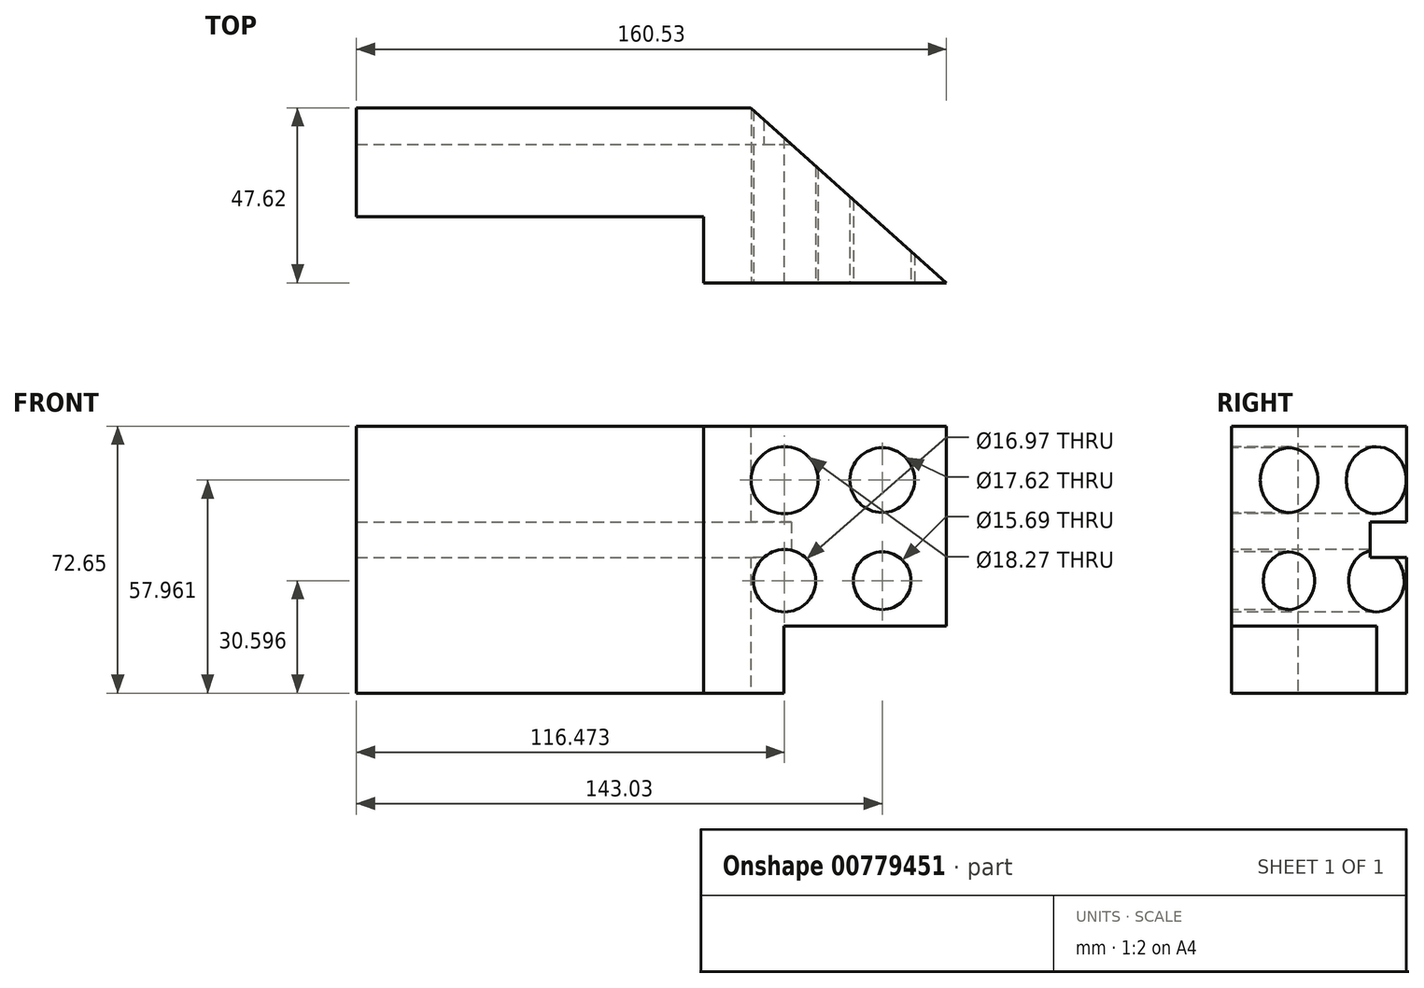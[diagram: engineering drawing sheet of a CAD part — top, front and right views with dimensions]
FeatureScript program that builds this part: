
annotation { "Feature Type Name" : "Feature", "Feature Type Description" : "" }
export const myFeature = defineFeature(function(context is Context, id is Id, definition is map)
    precondition{}
    {
        {
            var Q0;
            Q0=qCreatedBy(makeId("Top.planeOp"),FACE);
            var sketch = newSketch(context, id + "F0", { "sketchPlane" : qUnion([Q0])});
            skLineSegment(sketch, "E0.bottom", {"start": v(-53.64, 23.81) * mm, "end": v(53.64, 23.81) * mm});
            skLineSegment(sketch, "E0.top", {"start": v(-53.64, -23.81) * mm, "end": v(53.64, -23.81) * mm});
            skLineSegment(sketch, "E0.left", {"start": v(-53.64, 23.81) * mm, "end": v(-53.64, -23.81) * mm});
            skPoint(sketch, "E0.middle", {"position": v(0, 0) * mm});
            skLineSegment(sketch, "E1", {"start": v(53.64, -23.81) * mm, "end": v(106.9, -23.81) * mm});
            skLineSegment(sketch, "E2", {"start": v(106.9, -23.81) * mm, "end": v(53.64, 23.81) * mm});
            skSolve(sketch);
        }
        {
            var Q0;
            Q0=makeQuery(id+"F0.imprint","IMPRINT",FACE,{"disambiguationData":[TD([[makeQuery(id+"F0.imprint","IMPRINT",EDGE,{"derivedFrom":sQuery(id+"F0.wireOp",EDGE,"E0.bottom")}),-1.0]])]});
            extrude(context, id + "F1", {"entities" : qUnion([Q0]), "depth" : 54.36 * mm, "offsetDistance" : 25.4 * mm});
        }
        {
            var Q0;
            Q0=makeQuery(id+"F1.opExtrude","SWEPT_FACE",FACE,{"disambiguationData":[OSD([sQuery(id+"F0.wireOp",EDGE,"E0.top"),sQuery(id+"F0.wireOp",EDGE,"E1")])]});
            var sketch = newSketch(context, id + "F2", { "sketchPlane" : qUnion([Q0])});
            skLineSegment(sketch, "E3.bottom", {"start": v(-53.64, 54.36) * mm, "end": v(40.83, 54.36) * mm});
            skLineSegment(sketch, "E3.top", {"start": v(-53.64, 0) * mm, "end": v(40.83, 0) * mm});
            skLineSegment(sketch, "E3.left", {"start": v(-53.64, 54.36) * mm, "end": v(-53.64, 0) * mm});
            skLineSegment(sketch, "E3.right", {"start": v(40.83, 54.36) * mm, "end": v(40.83, 0) * mm});
            skSolve(sketch);
        }
        {
            var Q0;
            Q0=makeQuery(id+"F2.imprint","IMPRINT",FACE,{"disambiguationData":[TD([[makeQuery(id+"F2.imprint","IMPRINT",EDGE,{"derivedFrom":sQuery(id+"F2.wireOp",EDGE,"E3.bottom")}),-1.0]])]});
            extrude(context, id + "F3", {"entities" : qUnion([Q0]), "operationType" : NewBodyOperationType.REMOVE, "oppositeDirection" : true, "depth" : 18.03 * mm, "offsetDistance" : 25.4 * mm});
        }
        {
            var Q0;
            Q0=makeQuery(id+"F1.opExtrude","SWEPT_FACE",FACE,{"disambiguationData":[OSD([sQuery(id+"F0.wireOp",EDGE,"E0.top"),sQuery(id+"F0.wireOp",EDGE,"E1")])]});
            var sketch = newSketch(context, id + "F4", { "sketchPlane" : qUnion([Q0])});
            skPoint(sketch, "E4.middle", {"position": v(76.11, 25.99) * mm});
            skCircle(sketch, "E5", {"center": v(89.39, 39.67) * mm, "radius": 8.8 * mm});
            skCircle(sketch, "E6", {"center": v(89.39, 12.3) * mm, "radius": 7.85 * mm});
            skCircle(sketch, "E7", {"center": v(62.83, 12.3) * mm, "radius": 8.48 * mm});
            skCircle(sketch, "E8", {"center": v(62.83, 39.67) * mm, "radius": 9.14 * mm});
            skSolve(sketch);
        }
        {
            var Q0;
            Q0=makeQuery(id+"F4.imprint","IMPRINT",FACE,{"disambiguationData":[TD([[makeQuery(id+"F4.imprint","IMPRINT",EDGE,{"derivedFrom":sQuery(id+"F4.wireOp",EDGE,"E5")}),1.0]])]});
            var Q1;
            Q1=makeQuery(id+"F4.imprint","IMPRINT",FACE,{"disambiguationData":[TD([[makeQuery(id+"F4.imprint","IMPRINT",EDGE,{"derivedFrom":sQuery(id+"F4.wireOp",EDGE,"E6")}),1.0]])]});
            var Q2;
            Q2=makeQuery(id+"F4.imprint","IMPRINT",FACE,{"disambiguationData":[TD([[makeQuery(id+"F4.imprint","IMPRINT",EDGE,{"derivedFrom":sQuery(id+"F4.wireOp",EDGE,"E7")}),1.0]])]});
            var Q3;
            Q3=makeQuery(id+"F4.imprint","IMPRINT",FACE,{"disambiguationData":[TD([[makeQuery(id+"F4.imprint","IMPRINT",EDGE,{"derivedFrom":sQuery(id+"F4.wireOp",EDGE,"E8")}),1.0]])]});
            extrude(context, id + "F5", {"entities" : qUnion([Q0, Q1, Q2, Q3]), "operationType" : NewBodyOperationType.REMOVE, "oppositeDirection" : true, "depth" : 191.26 * mm, "offsetDistance" : 25.4 * mm});
        }
        {
            var Q0;
            Q0=makeQuery(id+"F1.opExtrude","CAP_FACE",FACE,{"disambiguationData":[OSD([sQuery(id+"F0.wireOp",EDGE,"E0.bottom"),sQuery(id+"F0.wireOp",EDGE,"E0.top"),sQuery(id+"F0.wireOp",EDGE,"E0.left"),sQuery(id+"F0.wireOp",EDGE,"E1"),sQuery(id+"F0.wireOp",EDGE,"E2")])],"isStart":true});
            var sketch = newSketch(context, id + "F6", { "sketchPlane" : qUnion([Q0])});
            skLineSegment(sketch, "E9", {"start": v(53.64, -23.81) * mm, "end": v(62.68, -15.73) * mm});
            skLineSegment(sketch, "E10", {"start": v(62.68, -15.73) * mm, "end": v(62.68, 23.81) * mm});
            skLineSegment(sketch, "E11", {"start": v(62.68, 23.81) * mm, "end": v(40.83, 23.81) * mm});
            skLineSegment(sketch, "E12", {"start": v(40.83, 23.81) * mm, "end": v(40.83, 5.78) * mm});
            skLineSegment(sketch, "E13", {"start": v(40.83, 5.78) * mm, "end": v(-53.64, 5.78) * mm});
            skLineSegment(sketch, "E14", {"start": v(-53.64, 5.78) * mm, "end": v(-53.64, -23.81) * mm});
            skLineSegment(sketch, "E15", {"start": v(-53.64, -23.81) * mm, "end": v(53.64, -23.81) * mm});
            skSolve(sketch);
        }
        {
            var Q0;
            Q0=makeQuery(id+"F6.imprint","IMPRINT",FACE,{"disambiguationData":[TD([[makeQuery(id+"F6.imprint","IMPRINT",EDGE,{"derivedFrom":sQuery(id+"F6.wireOp",EDGE,"E9")}),-1.0]])]});
            extrude(context, id + "F7", {"entities" : qUnion([Q0]), "operationType" : NewBodyOperationType.ADD, "depth" : 18.29 * mm, "offsetDistance" : 25.4 * mm});
        }
        {
            var Q0;
            Q0=makeQuery(id+"F7.boolean.opBoolean","MERGE",FACE,{"derivedFrom":[makeQuery(id+"F1.opExtrude","SWEPT_FACE",FACE,{"disambiguationData":[OSD([sQuery(id+"F0.wireOp",EDGE,"E0.bottom")])]}),makeQuery(id+"F7.opExtrude","SWEPT_FACE",FACE,{"disambiguationData":[OSD([sQuery(id+"F6.wireOp",EDGE,"E15")])]})]});
            var sketch = newSketch(context, id + "F8", { "sketchPlane" : qUnion([Q0])});
            skLineSegment(sketch, "E16.bottom", {"start": v(53.64, 28.25) * mm, "end": v(-160.92, 28.25) * mm});
            skLineSegment(sketch, "E16.top", {"start": v(53.64, 18.67) * mm, "end": v(-160.92, 18.67) * mm});
            skLineSegment(sketch, "E16.left", {"start": v(53.64, 28.25) * mm, "end": v(53.64, 18.67) * mm});
            skLineSegment(sketch, "E16.right", {"start": v(-160.92, 28.25) * mm, "end": v(-160.92, 18.67) * mm});
            skPoint(sketch, "E16.middle", {"position": v(-53.64, 23.46) * mm});
            skSolve(sketch);
        }
        {
            var Q0;
            {var subQ0=sQuery(id+"F8.wireOp",EDGE,"E16.right");Q0=makeQuery(id+"F8.imprint","IMPRINT",FACE,{"disambiguationData":[TD([[makeQuery(id+"F8.imprint","IMPRINT",EDGE,{"derivedFrom":subQ0}),1.0]])]});}
            var Q1;
            {var subQ0=sQuery(id+"F8.wireOp",EDGE,"E16.left");Q1=makeQuery(id+"F8.imprint","IMPRINT",FACE,{"disambiguationData":[TD([[makeQuery(id+"F8.imprint","IMPRINT",EDGE,{"derivedFrom":subQ0}),-1.0]])]});}
            extrude(context, id + "F9", {"entities" : qUnion([Q0, Q1]), "operationType" : NewBodyOperationType.REMOVE, "oppositeDirection" : true, "depth" : 9.9 * mm, "offsetDistance" : 25.4 * mm});
        }
    });
